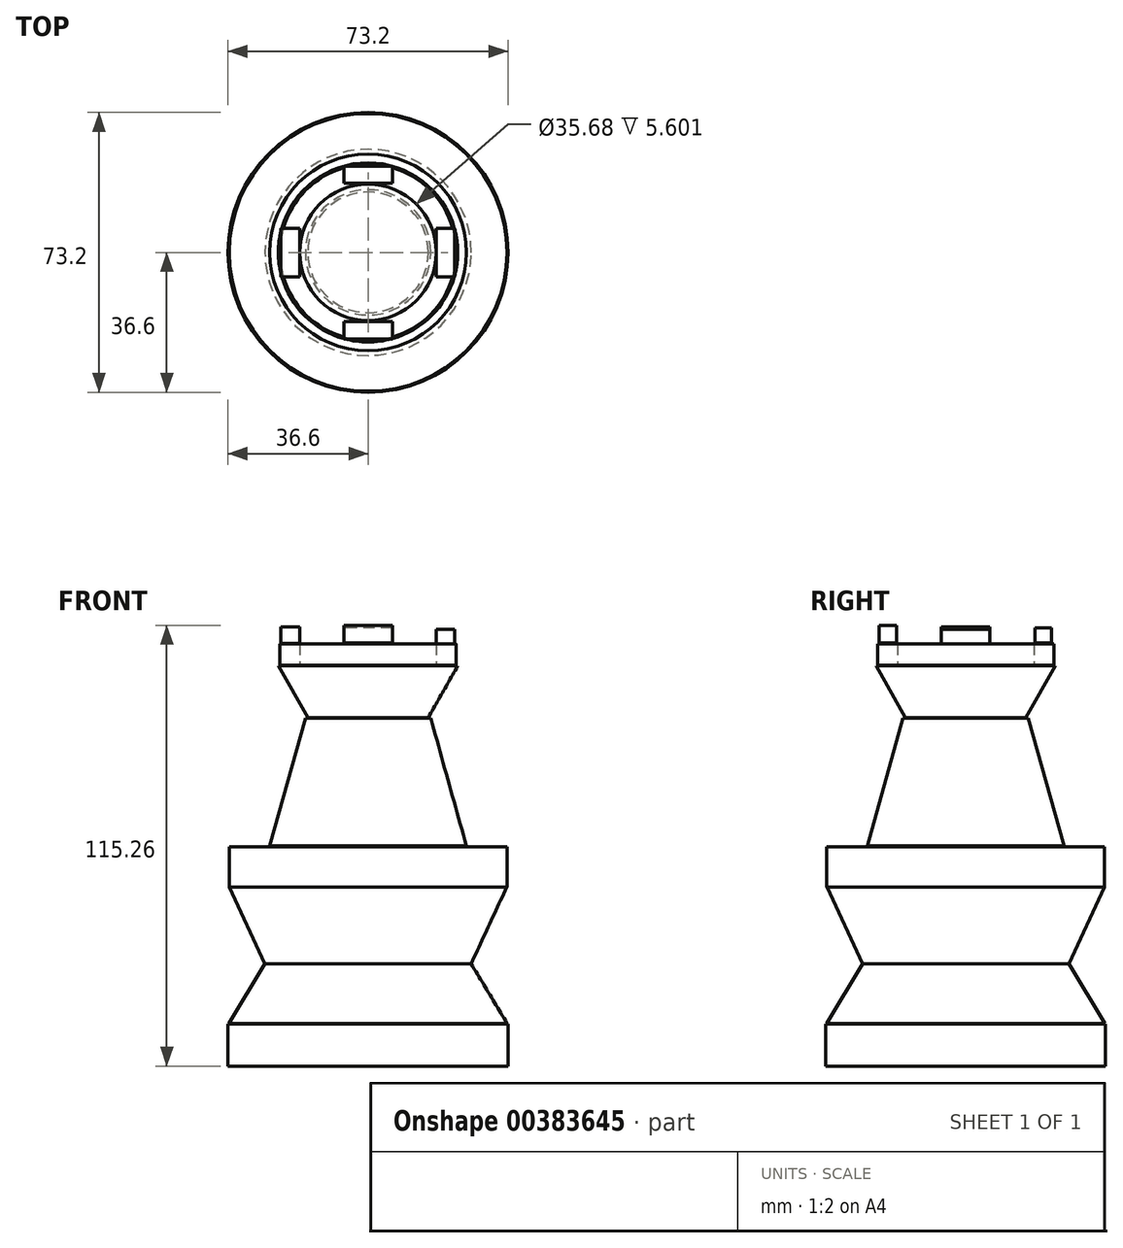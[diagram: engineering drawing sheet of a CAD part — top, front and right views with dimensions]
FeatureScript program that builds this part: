
annotation { "Feature Type Name" : "Feature", "Feature Type Description" : "" }
export const myFeature = defineFeature(function(context is Context, id is Id, definition is map)
    precondition{}
    {
        {
            var Q0;
            Q0=qCreatedBy(makeId("Front.planeOp"),FACE);
            var sketch = newSketch(context, id + "F0", { "sketchPlane" : qUnion([Q0])});
            skLineSegment(sketch, "E0.bottom", {"start": v(-36.6, -46.8) * mm, "end": v(0, -46.8) * mm});
            skLineSegment(sketch, "E0.top", {"start": v(-36.6, -35.78) * mm, "end": v(0, -35.78) * mm});
            skLineSegment(sketch, "E0.left", {"start": v(-36.6, -46.8) * mm, "end": v(-36.6, -35.78) * mm});
            skLineSegment(sketch, "E0.right", {"start": v(0, -46.8) * mm, "end": v(0, -35.78) * mm});
            skSolve(sketch);
        }
        {
            var Q0;
            Q0=makeQuery(id+"F0.imprint","IMPRINT",FACE,{"disambiguationData":[TD([[makeQuery(id+"F0.imprint","IMPRINT",EDGE,{"derivedFrom":sQuery(id+"F0.wireOp",EDGE,"E0.bottom")}),1.0]])]});
            var Q1;
            Q1=sQuery(id+"F0.wireOp",EDGE,"E0.right");
            revolve(context, id + "F1", {"entities" : qUnion([Q0]), "axis" : qUnion([Q1]), "revolveType" : RevolveType.FULL});
        }
        {
            var Q0;
            Q0=qCreatedBy(makeId("Front.planeOp"),FACE);
            var sketch = newSketch(context, id + "F2", { "sketchPlane" : qUnion([Q0])});
            skLineSegment(sketch, "E1", {"start": v(0, 0) * mm, "end": v(0, -35.63) * mm});
            skLineSegment(sketch, "E2", {"start": v(0, -35.63) * mm, "end": v(36.36, -35.63) * mm});
            skLineSegment(sketch, "E3", {"start": v(36.36, -35.63) * mm, "end": v(26.97, -20.05) * mm});
            skLineSegment(sketch, "E4", {"start": v(26.97, -20.05) * mm, "end": v(36.24, 0) * mm});
            skLineSegment(sketch, "E5", {"start": v(36.24, 0) * mm, "end": v(0, 0) * mm});
            skSolve(sketch);
        }
        {
            var Q0;
            Q0=makeQuery(id+"F2.imprint","IMPRINT",FACE,{"disambiguationData":[TD([[makeQuery(id+"F2.imprint","IMPRINT",EDGE,{"derivedFrom":sQuery(id+"F2.wireOp",EDGE,"E1")}),1.0]])]});
            var Q1;
            Q1=sQuery(id+"F2.wireOp",EDGE,"E1");
            revolve(context, id + "F3", {"entities" : qUnion([Q0]), "axis" : qUnion([Q1]), "revolveType" : RevolveType.FULL});
        }
        {
            var Q0;
            Q0=qCreatedBy(makeId("Front.planeOp"),FACE);
            var sketch = newSketch(context, id + "F4", { "sketchPlane" : qUnion([Q0])});
            skLineSegment(sketch, "E6.bottom", {"start": v(-36.3, 0) * mm, "end": v(0, 0) * mm});
            skLineSegment(sketch, "E6.top", {"start": v(-36.3, 10.58) * mm, "end": v(0, 10.58) * mm});
            skLineSegment(sketch, "E6.left", {"start": v(-36.3, 0) * mm, "end": v(-36.3, 10.58) * mm});
            skLineSegment(sketch, "E6.right", {"start": v(0, 0) * mm, "end": v(0, 10.58) * mm});
            skSolve(sketch);
        }
        {
            var Q0;
            Q0=makeQuery(id+"F4.imprint","IMPRINT",FACE,{"disambiguationData":[TD([[makeQuery(id+"F4.imprint","IMPRINT",EDGE,{"derivedFrom":sQuery(id+"F4.wireOp",EDGE,"E6.bottom")}),1.0]])]});
            var Q1;
            Q1=sQuery(id+"F4.wireOp",EDGE,"E6.right");
            revolve(context, id + "F5", {"operationType" : NewBodyOperationType.ADD, "entities" : qUnion([Q0]), "axis" : qUnion([Q1]), "revolveType" : RevolveType.FULL});
        }
        {
            var Q0;
            Q0=qCreatedBy(makeId("Front.planeOp"),FACE);
            var sketch = newSketch(context, id + "F6", { "sketchPlane" : qUnion([Q0])});
            skLineSegment(sketch, "E7", {"start": v(-25.72, 10.79) * mm, "end": v(-16.39, 44.19) * mm});
            skLineSegment(sketch, "E8", {"start": v(-16.39, 44.19) * mm, "end": v(0, 44.19) * mm});
            skLineSegment(sketch, "E9", {"start": v(0, 44.19) * mm, "end": v(0, 10.58) * mm});
            skLineSegment(sketch, "E10", {"start": v(0, 10.58) * mm, "end": v(-25.72, 10.79) * mm});
            skSolve(sketch);
        }
        {
            var Q0;
            Q0=makeQuery(id+"F6.imprint","IMPRINT",FACE,{"disambiguationData":[TD([[makeQuery(id+"F6.imprint","IMPRINT",EDGE,{"derivedFrom":sQuery(id+"F6.wireOp",EDGE,"E7")}),-1.0]])]});
            var Q1;
            Q1=sQuery(id+"F6.wireOp",EDGE,"E9");
            revolve(context, id + "F7", {"entities" : qUnion([Q0]), "axis" : qUnion([Q1]), "revolveType" : RevolveType.FULL});
        }
        {
            var Q0;
            Q0=qCreatedBy(makeId("Front.planeOp"),FACE);
            var sketch = newSketch(context, id + "F8", { "sketchPlane" : qUnion([Q0])});
            skLineSegment(sketch, "E11", {"start": v(0, 44.4) * mm, "end": v(15.77, 44.4) * mm});
            skLineSegment(sketch, "E12", {"start": v(15.77, 44.4) * mm, "end": v(23.44, 57.88) * mm});
            skLineSegment(sketch, "E13", {"start": v(23.44, 57.88) * mm, "end": v(0, 57.88) * mm});
            skLineSegment(sketch, "E14", {"start": v(0, 57.88) * mm, "end": v(0, 44.4) * mm});
            skSolve(sketch);
        }
        {
            var Q0;
            Q0=makeQuery(id+"F8.imprint","IMPRINT",FACE,{"disambiguationData":[TD([[makeQuery(id+"F8.imprint","IMPRINT",EDGE,{"derivedFrom":sQuery(id+"F8.wireOp",EDGE,"E11")}),1.0]])]});
            var Q1;
            Q1=sQuery(id+"F8.wireOp",EDGE,"E14");
            revolve(context, id + "F9", {"entities" : qUnion([Q0]), "axis" : qUnion([Q1]), "revolveType" : RevolveType.FULL});
        }
        {
            var Q0;
            Q0=qCreatedBy(makeId("Front.planeOp"),FACE);
            var sketch = newSketch(context, id + "F10", { "sketchPlane" : qUnion([Q0])});
            skLineSegment(sketch, "E15.bottom", {"start": v(-23.03, 58.09) * mm, "end": v(-17.84, 58.09) * mm});
            skLineSegment(sketch, "E15.top", {"start": v(-23.03, 63.69) * mm, "end": v(-17.84, 63.69) * mm});
            skLineSegment(sketch, "E15.left", {"start": v(-23.03, 58.09) * mm, "end": v(-23.03, 63.69) * mm});
            skLineSegment(sketch, "E15.right", {"start": v(-17.84, 58.09) * mm, "end": v(-17.84, 63.69) * mm});
            skSolve(sketch);
        }
        {
            var Q0;
            Q0=makeQuery(id+"F10.imprint","IMPRINT",FACE,{"disambiguationData":[TD([[makeQuery(id+"F10.imprint","IMPRINT",EDGE,{"derivedFrom":sQuery(id+"F10.wireOp",EDGE,"E15.bottom")}),1.0]])]});
            var Q1;
            Q1=makeQuery(id+"F7.opRevolve","SWEPT_EDGE",EDGE,{"disambiguationData":[OSD([sQuery(id+"F6.wireOp",EDGE,"E7"),sQuery(id+"F6.wireOp",EDGE,"E8")])]});
            revolve(context, id + "F11", {"entities" : qUnion([Q0]), "axis" : qUnion([Q1]), "revolveType" : RevolveType.FULL});
        }
        {
            var Q0;
            Q0=qCreatedBy(makeId("Front.planeOp"),FACE);
            var sketch = newSketch(context, id + "F12", { "sketchPlane" : qUnion([Q0])});
            skLineSegment(sketch, "E16.bottom", {"start": v(-22.77, 63.78) * mm, "end": v(-17.93, 63.78) * mm});
            skLineSegment(sketch, "E16.top", {"start": v(-22.77, 68.06) * mm, "end": v(-17.93, 68.06) * mm});
            skLineSegment(sketch, "E16.left", {"start": v(-22.77, 63.78) * mm, "end": v(-22.77, 68.06) * mm});
            skLineSegment(sketch, "E16.right", {"start": v(-17.93, 63.78) * mm, "end": v(-17.93, 68.06) * mm});
            skSolve(sketch);
        }
        {
            var Q0;
            Q0=makeQuery(id+"F12.imprint","IMPRINT",FACE,{"disambiguationData":[TD([[makeQuery(id+"F12.imprint","IMPRINT",EDGE,{"derivedFrom":sQuery(id+"F12.wireOp",EDGE,"E16.bottom")}),1.0]])]});
            extrude(context, id + "F13", {"entities" : qUnion([Q0]), "endBound" : BoundingType.SYMMETRIC, "oppositeDirection" : true, "depth" : 12.7 * mm});
        }
        {
            var Q0;
            Q0=qCreatedBy(makeId("Front.planeOp"),FACE);
            var sketch = newSketch(context, id + "F14", { "sketchPlane" : qUnion([Q0])});
            skLineSegment(sketch, "E17.bottom", {"start": v(22.61, 63.69) * mm, "end": v(17.84, 63.69) * mm});
            skLineSegment(sketch, "E17.top", {"start": v(22.61, 67.42) * mm, "end": v(17.84, 67.42) * mm});
            skLineSegment(sketch, "E17.left", {"start": v(22.61, 63.69) * mm, "end": v(22.61, 67.42) * mm});
            skLineSegment(sketch, "E17.right", {"start": v(17.84, 63.69) * mm, "end": v(17.84, 67.42) * mm});
            skSolve(sketch);
        }
        {
            var Q0;
            Q0=makeQuery(id+"F14.imprint","IMPRINT",FACE,{"disambiguationData":[TD([[makeQuery(id+"F14.imprint","IMPRINT",EDGE,{"derivedFrom":sQuery(id+"F14.wireOp",EDGE,"E17.bottom")}),-1.0]])]});
            extrude(context, id + "F15", {"entities" : qUnion([Q0]), "operationType" : NewBodyOperationType.ADD, "endBound" : BoundingType.SYMMETRIC, "depth" : 12.7 * mm});
        }
        {
            var Q0;
            Q0=qCreatedBy(makeId("Right.planeOp"),FACE);
            var sketch = newSketch(context, id + "F16", { "sketchPlane" : qUnion([Q0])});
            skLineSegment(sketch, "E18.bottom", {"start": v(22.5, 63.95) * mm, "end": v(18.13, 63.95) * mm});
            skLineSegment(sketch, "E18.top", {"start": v(22.5, 67.85) * mm, "end": v(18.13, 67.85) * mm});
            skLineSegment(sketch, "E18.left", {"start": v(22.5, 63.95) * mm, "end": v(22.5, 67.85) * mm});
            skLineSegment(sketch, "E18.right", {"start": v(18.13, 63.95) * mm, "end": v(18.13, 67.85) * mm});
            skSolve(sketch);
        }
        {
            var Q0;
            Q0=makeQuery(id+"F16.imprint","IMPRINT",FACE,{"disambiguationData":[TD([[makeQuery(id+"F16.imprint","IMPRINT",EDGE,{"derivedFrom":sQuery(id+"F16.wireOp",EDGE,"E18.bottom")}),-1.0]])]});
            var sketch = newSketch(context, id + "F17", { "sketchPlane" : qUnion([Q0])});
            skSolve(sketch);
        }
        {
            var Q0;
            Q0=makeQuery(id+"F17.imprint","IMPRINT",FACE,{"disambiguationData":[TD([[makeQuery(id+"F17.imprint","IMPRINT",EDGE,{"derivedFrom":makeQuery(id+"F16.imprint","IMPRINT",EDGE,{"derivedFrom":sQuery(id+"F16.wireOp",EDGE,"E18.bottom")})}),-1.0]])]});
            var sketch = newSketch(context, id + "F18", { "sketchPlane" : qUnion([Q0])});
            skSolve(sketch);
        }
        {
            var Q0;
            Q0=makeQuery(id+"F18.imprint","IMPRINT",FACE,{"disambiguationData":[TD([[makeQuery(id+"F18.imprint","IMPRINT",EDGE,{"derivedFrom":makeQuery(id+"F17.imprint","IMPRINT",EDGE,{"derivedFrom":makeQuery(id+"F16.imprint","IMPRINT",EDGE,{"derivedFrom":sQuery(id+"F16.wireOp",EDGE,"E18.bottom")})})}),-1.0]])]});
            extrude(context, id + "F19", {"entities" : qUnion([Q0]), "endBound" : BoundingType.SYMMETRIC, "depth" : 12.7 * mm});
        }
        {
            var Q0;
            Q0=qCreatedBy(makeId("Right.planeOp"),FACE);
            var sketch = newSketch(context, id + "F20", { "sketchPlane" : qUnion([Q0])});
            skLineSegment(sketch, "E19.bottom", {"start": v(-22.61, 63.9) * mm, "end": v(-18.05, 63.9) * mm});
            skLineSegment(sketch, "E19.top", {"start": v(-22.61, 68.46) * mm, "end": v(-18.05, 68.46) * mm});
            skLineSegment(sketch, "E19.left", {"start": v(-22.61, 63.9) * mm, "end": v(-22.61, 68.46) * mm});
            skLineSegment(sketch, "E19.right", {"start": v(-18.05, 63.9) * mm, "end": v(-18.05, 68.46) * mm});
            skSolve(sketch);
        }
        {
            var Q0;
            Q0=makeQuery(id+"F20.imprint","IMPRINT",FACE,{"disambiguationData":[TD([[makeQuery(id+"F20.imprint","IMPRINT",EDGE,{"derivedFrom":sQuery(id+"F20.wireOp",EDGE,"E19.bottom")}),1.0]])]});
            extrude(context, id + "F21", {"entities" : qUnion([Q0]), "endBound" : BoundingType.SYMMETRIC, "depth" : 12.7 * mm});
        }
    });
